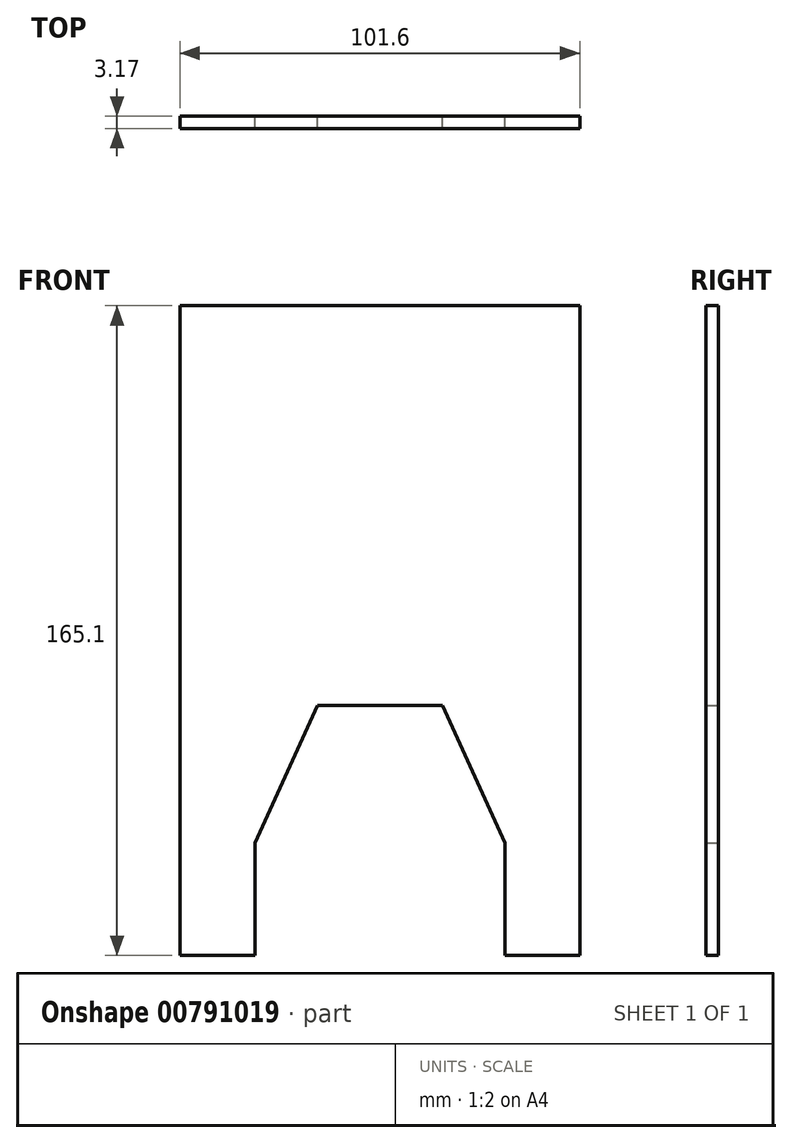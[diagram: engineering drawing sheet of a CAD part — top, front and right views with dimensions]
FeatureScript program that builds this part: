
annotation { "Feature Type Name" : "Feature", "Feature Type Description" : "" }
export const myFeature = defineFeature(function(context is Context, id is Id, definition is map)
    precondition{}
    {
        {
            var Q0;
            Q0=qCreatedBy(makeId("Front.planeOp"),FACE);
            var sketch = newSketch(context, id + "F0", { "sketchPlane" : qUnion([Q0])});
            skLineSegment(sketch, "E0.bottom", {"start": v(-50.8, 78.26) * mm, "end": v(50.8, 78.26) * mm});
            skLineSegment(sketch, "E0.top", {"start": v(-50.8, -86.84) * mm, "end": v(50.8, -86.84) * mm});
            skLineSegment(sketch, "E0.left", {"start": v(-50.8, 78.26) * mm, "end": v(-50.8, -86.84) * mm});
            skLineSegment(sketch, "E0.right", {"start": v(50.8, 78.26) * mm, "end": v(50.8, -86.84) * mm});
            skPoint(sketch, "E0.middle", {"position": v(0, -4.3) * mm});
            skLineSegment(sketch, "E1", {"start": v(-31.75, -86.84) * mm, "end": v(-31.75, -58.27) * mm});
            skLineSegment(sketch, "E2.MirrorCS", {"start": v(31.75, -86.84) * mm, "end": v(31.75, -58.27) * mm});
            skLineSegment(sketch, "E3", {"start": v(-15.88, -23.34) * mm, "end": v(15.88, -23.34) * mm});
            skLineSegment(sketch, "E4", {"start": v(-15.88, -23.34) * mm, "end": v(-31.75, -58.27) * mm});
            skLineSegment(sketch, "E5.MirrorCS", {"start": v(15.88, -23.34) * mm, "end": v(31.75, -58.27) * mm});
            skPoint(sketch, "E6.orphan", {"position": v(-31.75, -23.34) * mm});
            skPoint(sketch, "E7.orphan", {"position": v(31.75, -23.34) * mm});
            skCircle(sketch, "E8", {"center": v(0, -58.08) * mm, "radius": 28.29 * mm});
            skSolve(sketch);
        }
        {
            var Q0;
            Q0=makeQuery(id+"F0.imprint","IMPRINT",FACE,{"disambiguationData":[TD([[makeQuery(id+"F0.imprint","IMPRINT",EDGE,{"derivedFrom":sQuery(id+"F0.wireOp",EDGE,"E0.bottom")}),-1.0]])]});
            extrude(context, id + "F1", {"entities" : qUnion([Q0]), "depth" : 3.17 * mm, "offsetDistance" : 25.4 * mm});
        }
    });
